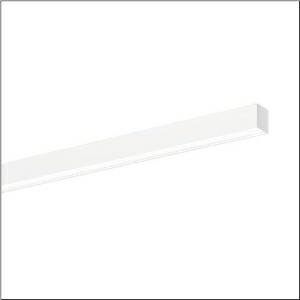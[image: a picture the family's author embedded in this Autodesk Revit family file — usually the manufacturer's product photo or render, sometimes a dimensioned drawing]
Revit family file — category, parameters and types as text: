
# Revit family: silica_r__21_51mx23da34wb_c22c
name_source: partatom
category: Lighting Fixtures
units: mm (PartAtom-declared; Revit-internal decimal feet)

## family parameters
Cut with Voids When Loaded = No
Host = Face
Light Source = No
Part Type = Normal
Room Calculation Point = No
Round Connector Dimension = Use Diameter
Shared = No

## types (1)
- --- (1 x LED, 3280 lm, 24.1 W, 3000K)
    Apparent Load = 24 VA
    CIE Flux Codes = 78 96 99 100 100
    Color Rendering = 80
    Color Temperature = 3000K
    Default Elevation = 1800 mm
    Description = Silica® 21, office luminaire, primary optical cover: prismatic diffuser, of PMMA, CAT 2 (L<= 3000cd/m²), light emission: direct distribution, primary light characteristic: symmetric, installation type: surface-mounted, LED, rated luminous flux: 3.280lm, luminous efficacy: 136lm/W, light colour: 830, colour temperature: 3000K, control gear: DALI 2, with terminal, 3+2-pole, max. 2.5mm², mains connection: 220..240V, AC, 50/60Hz, rated input power: 24.1W, luminaire housing, of aluminium, traffic white (RAL 9016), length: 1.204mm, width: 53mm, height: 53mm, protection rating (complete): IP20, insulation class (complete): insulation class I (protective earthing), certification: CE, permissible operating ambient temperature: 0..+35°C, standard: EN 50419, packaging unit: 1 piece
    Height = 53 mm
    Lamp = 1 x LED
    Lamp Light Flux = 3280 lm
    Lamp Power = 24.1 W
    Lamp count = 1
    Length = 1204 mm
    Luminous efficacy = 136 lm/W
    Manufacturer = Siteco
    ModVariant = No
    Model = 51MX23DA34WB
    Mounting Place = Ceiling
    Mounting Type = Surface mounted
    Number of Poles = 1
    OnlyDefault = Yes
    Power Factor = 1
    Product Name = Silica® 21
    Product group = office luminaire | ceiling mounted
    ProductGroupID = 302
    Protection Class = Protection class I
    Protection Degree = IP 20
    RLX_Detail_Level = 1
    RLX_Emergency_Light_Flux = 0 lm
    RLX_Emergency_Type = 0
    RLX_Emergency_Type_DB = No
    RlxData = <blob elided: 18817 chars, md5=13f1c426>
    Socket = socket
    Standby Power = 0 W
    System Light Flux = 3280 lm
    System Power = 24 W
    Type Comments = factory setting: luminous flux: 100 % | dim-lin: 254 | 345 mA
    Type Image = l_1335877.jpg
    URL = http://relux.com
    VarID = @adj_007995
    Voltage = 0 V
    Weight = 0.00 kg
    Width = 53 mm

## geometry (parser evidence)
native form markers: Blend x4, Sweep x13
no freeform markers — native parametric forms only
